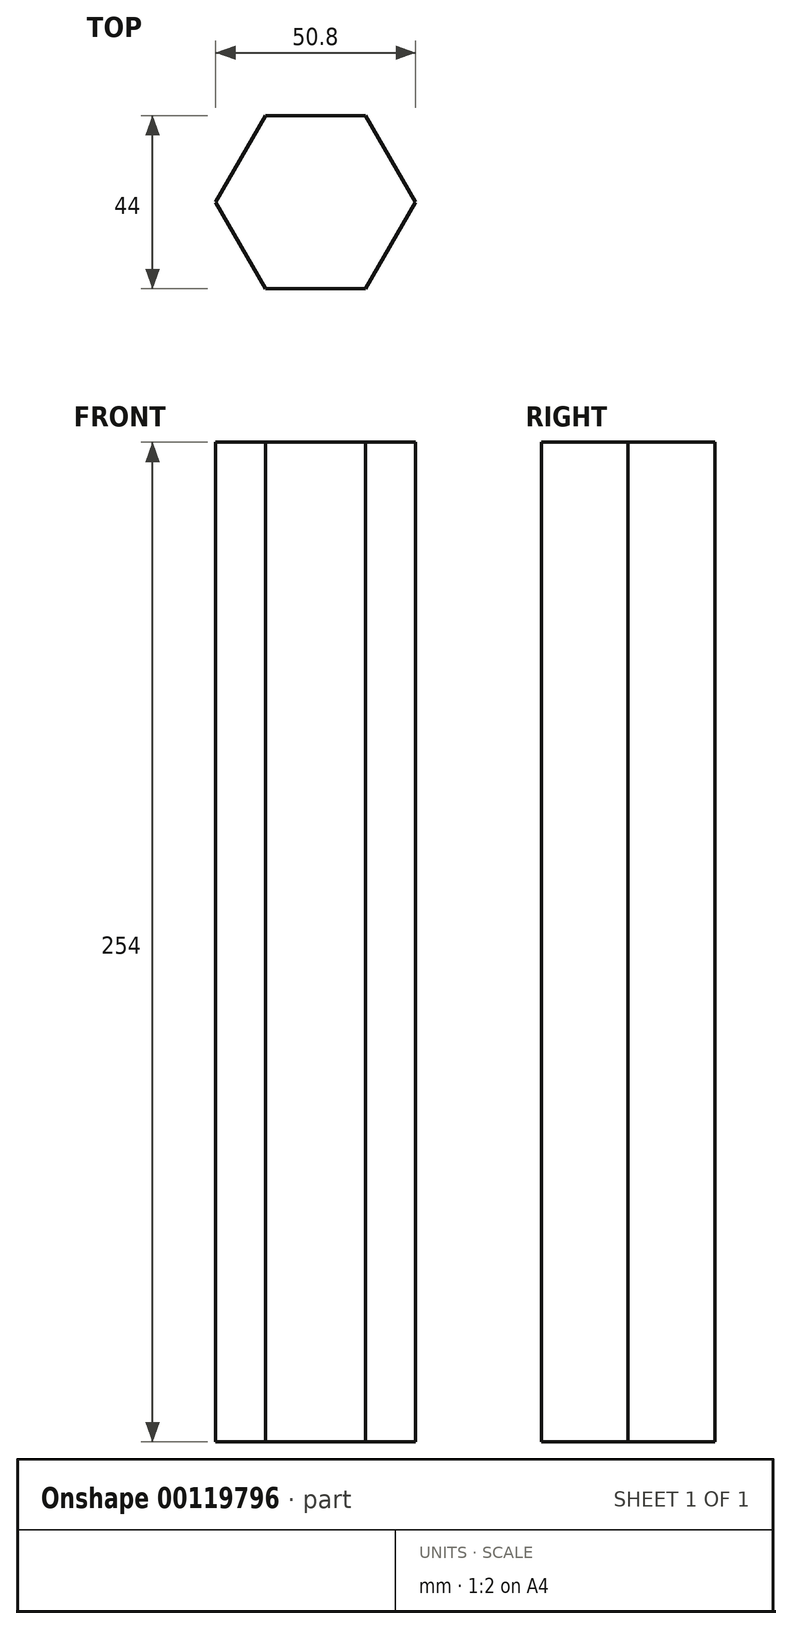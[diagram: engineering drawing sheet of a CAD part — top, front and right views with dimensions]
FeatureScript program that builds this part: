
annotation { "Feature Type Name" : "Feature", "Feature Type Description" : "" }
export const myFeature = defineFeature(function(context is Context, id is Id, definition is map)
    precondition{}
    {
        {
            var Q0;
            Q0=qCreatedBy(makeId("Top.planeOp"),FACE);
            var sketch = newSketch(context, id + "F0", { "sketchPlane" : qUnion([Q0])});
            skCircle(sketch, "E0.cCircle", {"center": v(-44.68, 30.37) * mm, "radius": 22 * mm, "construction": true});
            skLineSegment(sketch, "E0.0", {"start": v(-31.98, 52.37) * mm, "end": v(-19.28, 30.37) * mm});
            skLineSegment(sketch, "E0.1", {"start": v(-19.28, 30.37) * mm, "end": v(-31.98, 8.37) * mm});
            skLineSegment(sketch, "E0.2", {"start": v(-31.98, 8.37) * mm, "end": v(-57.38, 8.37) * mm});
            skLineSegment(sketch, "E0.3", {"start": v(-57.38, 8.37) * mm, "end": v(-70.08, 30.37) * mm});
            skLineSegment(sketch, "E0.4", {"start": v(-70.08, 30.37) * mm, "end": v(-57.38, 52.37) * mm});
            skLineSegment(sketch, "E0.5", {"start": v(-57.38, 52.37) * mm, "end": v(-31.98, 52.37) * mm});
            skPoint(sketch, "E0.0.midPoint", {"position": v(-25.63, 41.37) * mm});
            skSolve(sketch);
        }
        {
            var Q0;
            Q0 = qSketchRegion(id + "F0", true);
            extrude(context, id + "F1", {"entities" : qUnion([Q0]), "depth" : 254 * mm});
        }
    });
